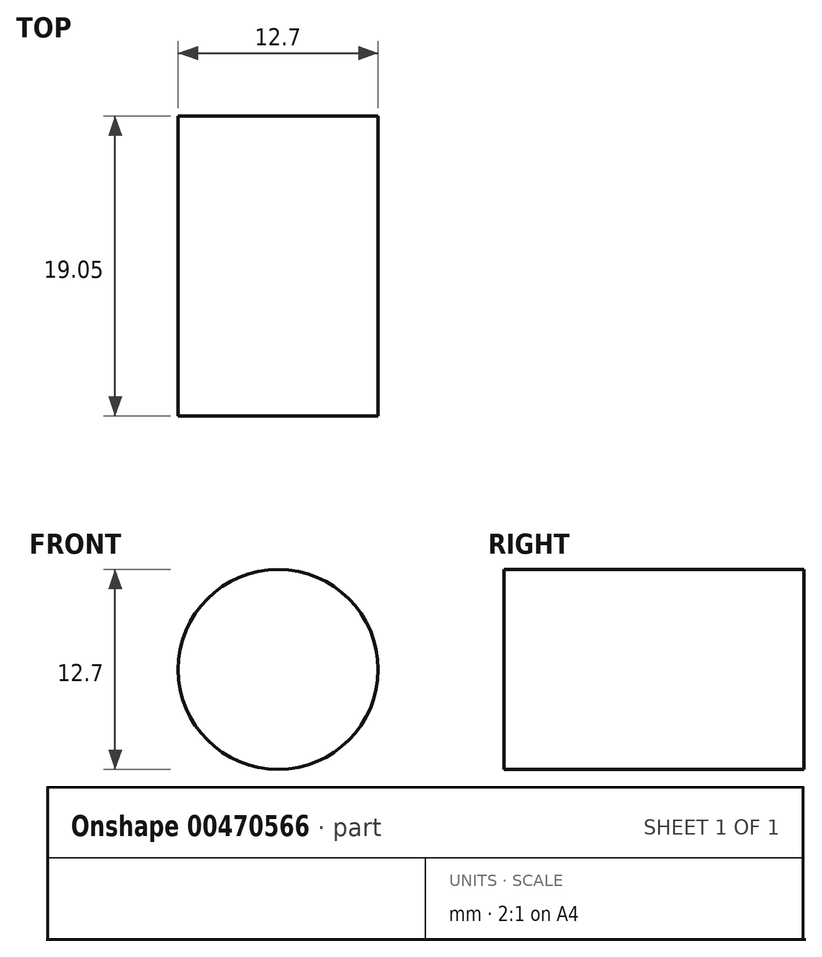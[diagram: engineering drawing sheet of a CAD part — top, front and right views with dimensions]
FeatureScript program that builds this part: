
annotation { "Feature Type Name" : "Feature", "Feature Type Description" : "" }
export const myFeature = defineFeature(function(context is Context, id is Id, definition is map)
    precondition{}
    {
        {
            var Q0;
            Q0=qCreatedBy(makeId("Front.planeOp"),FACE);
            var sketch = newSketch(context, id + "F0", { "sketchPlane" : qUnion([Q0])});
            skCircle(sketch, "E0", {"center": v(0, 0) * mm, "radius": 6.35 * mm});
            skSolve(sketch);
        }
        {
            var Q0;
            Q0=makeQuery(id+"F0.imprint","IMPRINT",FACE,{"disambiguationData":[TD([[makeQuery(id+"F0.imprint","IMPRINT",EDGE,{"derivedFrom":sQuery(id+"F0.wireOp",EDGE,"E0")}),1.0]])]});
            extrude(context, id + "F1", {"entities" : qUnion([Q0]), "depth" : 19.05 * mm});
        }
    });
